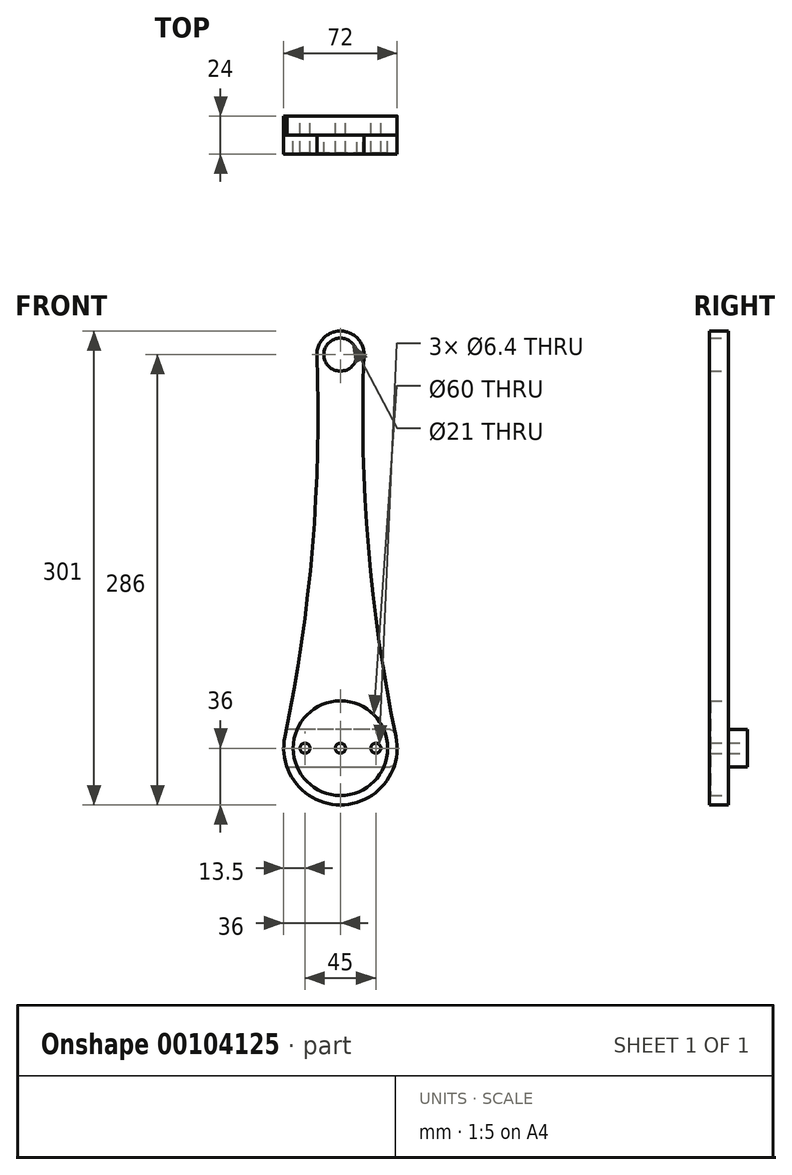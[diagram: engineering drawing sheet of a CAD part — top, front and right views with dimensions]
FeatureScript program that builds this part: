
annotation { "Feature Type Name" : "Feature", "Feature Type Description" : "" }
export const myFeature = defineFeature(function(context is Context, id is Id, definition is map)
    precondition{}
    {
        {
            var Q0;
            Q0=qCreatedBy(makeId("Front.planeOp"),FACE);
            var sketch = newSketch(context, id + "F0", { "sketchPlane" : qUnion([Q0])});
            skCircle(sketch, "E0", {"center": v(22.5, 0) * mm, "radius": 3.2 * mm});
            skCircle(sketch, "E1", {"center": v(-22.5, 0) * mm, "radius": 3.2 * mm});
            skLineSegment(sketch, "E2", {"start": v(0, 0) * mm, "end": v(0, 12.27) * mm, "construction": true});
            skCircle(sketch, "E3", {"center": v(0, 0) * mm, "radius": 36 * mm});
            skCircle(sketch, "E4", {"center": v(0, 0) * mm, "radius": 30 * mm});
            skCircle(sketch, "E5", {"center": v(0, 0) * mm, "radius": 3.2 * mm});
            skSolve(sketch);
        }
        {
            var Q0;
            Q0=makeQuery(id+"F2.opExtrude","CAP_FACE",FACE,{"disambiguationData":[OSD([sQuery(id+"F0.wireOp",EDGE,"E0"),sQuery(id+"F0.wireOp",EDGE,"E1"),sQuery(id+"F0.wireOp",EDGE,"E3")])],"isStart":true});
            var Q1;
            Q1=makeQuery(id+"F0.imprint","IMPRINT",FACE,{"disambiguationData":[TD([[makeQuery(id+"F0.imprint","IMPRINT",EDGE,{"derivedFrom":sQuery(id+"F0.wireOp",EDGE,"E0")}),-1.0]])]});
            extrude(context, id + "F1", {"entities" : qUnion([Q0, Q1]), "depth" : 23.5 * mm});
        }
        {
            var Q0;
            Q0 = qSketchRegion(id + "F0", true);
            var Q1;
            Q1=makeQuery(id+"F0.imprint","IMPRINT",FACE,{"disambiguationData":[TD([[makeQuery(id+"F0.imprint","IMPRINT",EDGE,{"derivedFrom":sQuery(id+"F0.wireOp",EDGE,"E0")}),-1.0]])]});
            extrude(context, id + "F2", {"entities" : qUnion([Q0, Q1]), "operationType" : NewBodyOperationType.ADD, "depth" : 12 * mm});
        }
        {
            var Q0;
            Q0=makeQuery(id+"F2.opExtrude","CAP_FACE",FACE,{"disambiguationData":[OSD([sQuery(id+"F0.wireOp",EDGE,"E0"),sQuery(id+"F0.wireOp",EDGE,"E1"),sQuery(id+"F0.wireOp",EDGE,"E3")])],"isStart":false});
            var sketch = newSketch(context, id + "F3", { "sketchPlane" : qUnion([Q0])});
            skArc(sketch, "E6.0", {"start": v(-35.24, 7.34) * mm, "mid": v(0, -36) * mm, "end": v(35.24, 7.34) * mm});
            skCircle(sketch, "E6.1", {"center": v(0, 0) * mm, "radius": 30 * mm});
            skCircle(sketch, "E7", {"center": v(0, 250) * mm, "radius": 10.5 * mm});
            skArc(sketch, "E8", {"start": v(14.99, 249.43) * mm, "mid": v(0, 265) * mm, "end": v(-14.99, 249.43) * mm});
            skArc(sketch, "E9", {"start": v(14.99, 249.43) * mm, "mid": v(17.74, 127.76) * mm, "end": v(35.24, 7.34) * mm});
            skLineSegment(sketch, "E10", {"start": v(0, 250) * mm, "end": v(0, 72.38) * mm, "construction": true});
            skArc(sketch, "E11.MirrorCS", {"start": v(-14.99, 249.43) * mm, "mid": v(-17.74, 127.76) * mm, "end": v(-35.24, 7.34) * mm});
            skSolve(sketch);
        }
        {
            var Q0;
            Q0 = qSketchRegion(id + "F3", true);
            extrude(context, id + "F4", {"entities" : qUnion([Q0]), "depth" : 12 * mm});
        }
        {
            var Q0;
            {var subQ0=sQuery(id+"F0.wireOp",EDGE,"E5");var subQ1=sQuery(id+"F0.wireOp",EDGE,"E1");var subQ2=sQuery(id+"F0.wireOp",EDGE,"E0");Q0=makeQuery(id+"F2.boolean.opBoolean","MERGE",FACE,{"derivedFrom":[makeQuery(id+"F1.opExtrude","CAP_FACE",FACE,{"disambiguationData":[OSD([subQ2,subQ1,sQuery(id+"F0.wireOp",EDGE,"E4"),subQ0])],"isStart":true}),makeQuery(id+"F2.opExtrude","CAP_FACE",FACE,{"disambiguationData":[OSD([subQ2,subQ1,sQuery(id+"F0.wireOp",EDGE,"E3"),subQ0])],"isStart":true})]});}
            var sketch = newSketch(context, id + "F5", { "sketchPlane" : qUnion([Q0])});
            skCircle(sketch, "E12.0", {"center": v(0, 0) * mm, "radius": 36 * mm});
            skLineSegment(sketch, "E13", {"start": v(-33.94, 12) * mm, "end": v(33.94, 12) * mm});
            skLineSegment(sketch, "E14", {"start": v(33.94, -12) * mm, "end": v(-33.94, -12) * mm});
            skLineSegment(sketch, "E15", {"start": v(-51.47, 0) * mm, "end": v(53.04, 0) * mm, "construction": true});
            skPoint(sketch, "E16.orphan", {"position": v(51.8, 12) * mm});
            skPoint(sketch, "E17.orphan", {"position": v(53.04, -12) * mm});
            skSolve(sketch);
        }
        {
            var Q0;
            Q0=makeQuery(id+"F5.imprint","IMPRINT",FACE,{"disambiguationData":[TD([[makeQuery(id+"F5.imprint","IMPRINT",EDGE,{"derivedFrom":makeQuery(id+"F1.opExtrude","CAP_EDGE",EDGE,{"disambiguationData":[OSD([sQuery(id+"F0.wireOp",EDGE,"E0")])],"isStart":true})}),-1.0]])]});
            var Q1;
            Q1=makeQuery(id+"F5.imprint","IMPRINT",FACE,{"disambiguationData":[TD([[makeQuery(id+"F5.imprint","IMPRINT",EDGE,{"derivedFrom":makeQuery(id+"F1.opExtrude","CAP_EDGE",EDGE,{"disambiguationData":[OSD([sQuery(id+"F0.wireOp",EDGE,"E1")])],"isStart":true})}),-1.0]])]});
            var Q2;
            Q2=makeQuery(id+"F5.imprint","IMPRINT",FACE,{"disambiguationData":[TD([[makeQuery(id+"F5.imprint","IMPRINT",EDGE,{"derivedFrom":makeQuery(id+"F1.opExtrude","CAP_EDGE",EDGE,{"disambiguationData":[OSD([sQuery(id+"F0.wireOp",EDGE,"E5")])],"isStart":true})}),-1.0]])]});
            var Q3;
            {var subQ0=sQuery(id+"F5.wireOp",EDGE,"E13");Q3=makeQuery(id+"F5.imprint","IMPRINT",FACE,{"disambiguationData":[TD([[makeQuery(id+"F5.imprint","IMPRINT",EDGE,{"derivedFrom":subQ0}),1.0]])]});}
            var Q4;
            {var subQ0=sQuery(id+"F5.wireOp",EDGE,"E14");Q4=makeQuery(id+"F5.imprint","IMPRINT",FACE,{"disambiguationData":[TD([[makeQuery(id+"F5.imprint","IMPRINT",EDGE,{"derivedFrom":subQ0}),1.0]])]});}
            extrude(context, id + "F6", {"entities" : qUnion([Q0, Q1, Q2, Q3, Q4]), "operationType" : NewBodyOperationType.REMOVE, "oppositeDirection" : true, "depth" : 12 * mm});
        }
        {
            var Q0;
            {var subQ0=sQuery(id+"F5.wireOp",EDGE,"E13");var subQ1=sQuery(id+"F5.wireOp",EDGE,"E12.0");Q0=makeQuery(id+"F6.boolean.opBoolean","COPY",EDGE,{"derivedFrom":makeQuery(id+"F6.opExtrude","SWEPT_EDGE",EDGE,{"disambiguationData":[OSD([subQ1,subQ0]),TDD([makeQuery(id+"F5.imprint","INTERSECT",VERTEX,{"disambiguationData":[OD(1.0)],"derivedFrom":[subQ1,subQ0]})])]})});}
            var Q1;
            {var subQ0=sQuery(id+"F5.wireOp",EDGE,"E13");var subQ1=sQuery(id+"F5.wireOp",EDGE,"E12.0");Q1=makeQuery(id+"F6.boolean.opBoolean","COPY",EDGE,{"derivedFrom":makeQuery(id+"F6.opExtrude","SWEPT_EDGE",EDGE,{"disambiguationData":[OSD([subQ1,subQ0]),TDD([makeQuery(id+"F5.imprint","INTERSECT",VERTEX,{"disambiguationData":[OD(0.0)],"derivedFrom":[subQ1,subQ0]})])]})});}
            var Q2;
            {var subQ0=sQuery(id+"F5.wireOp",EDGE,"E14");var subQ1=sQuery(id+"F5.wireOp",EDGE,"E12.0");Q2=makeQuery(id+"F6.boolean.opBoolean","COPY",EDGE,{"derivedFrom":makeQuery(id+"F6.opExtrude","SWEPT_EDGE",EDGE,{"disambiguationData":[OSD([subQ1,subQ0]),TDD([makeQuery(id+"F5.imprint","INTERSECT",VERTEX,{"disambiguationData":[OD(0.0)],"derivedFrom":[subQ1,subQ0]})])]})});}
            var Q3;
            {var subQ0=sQuery(id+"F5.wireOp",EDGE,"E14");var subQ1=sQuery(id+"F5.wireOp",EDGE,"E12.0");Q3=makeQuery(id+"F6.boolean.opBoolean","COPY",EDGE,{"derivedFrom":makeQuery(id+"F6.opExtrude","SWEPT_EDGE",EDGE,{"disambiguationData":[OSD([subQ1,subQ0]),TDD([makeQuery(id+"F5.imprint","INTERSECT",VERTEX,{"disambiguationData":[OD(1.0)],"derivedFrom":[subQ1,subQ0]})])]})});}
            fillet(context, id + "F7", {"entities" : qUnion([Q0, Q1, Q2, Q3]), "radius" : 5 * mm, "tangentPropagation" : true, "allowEdgeOverflow" : false});
        }
    });
